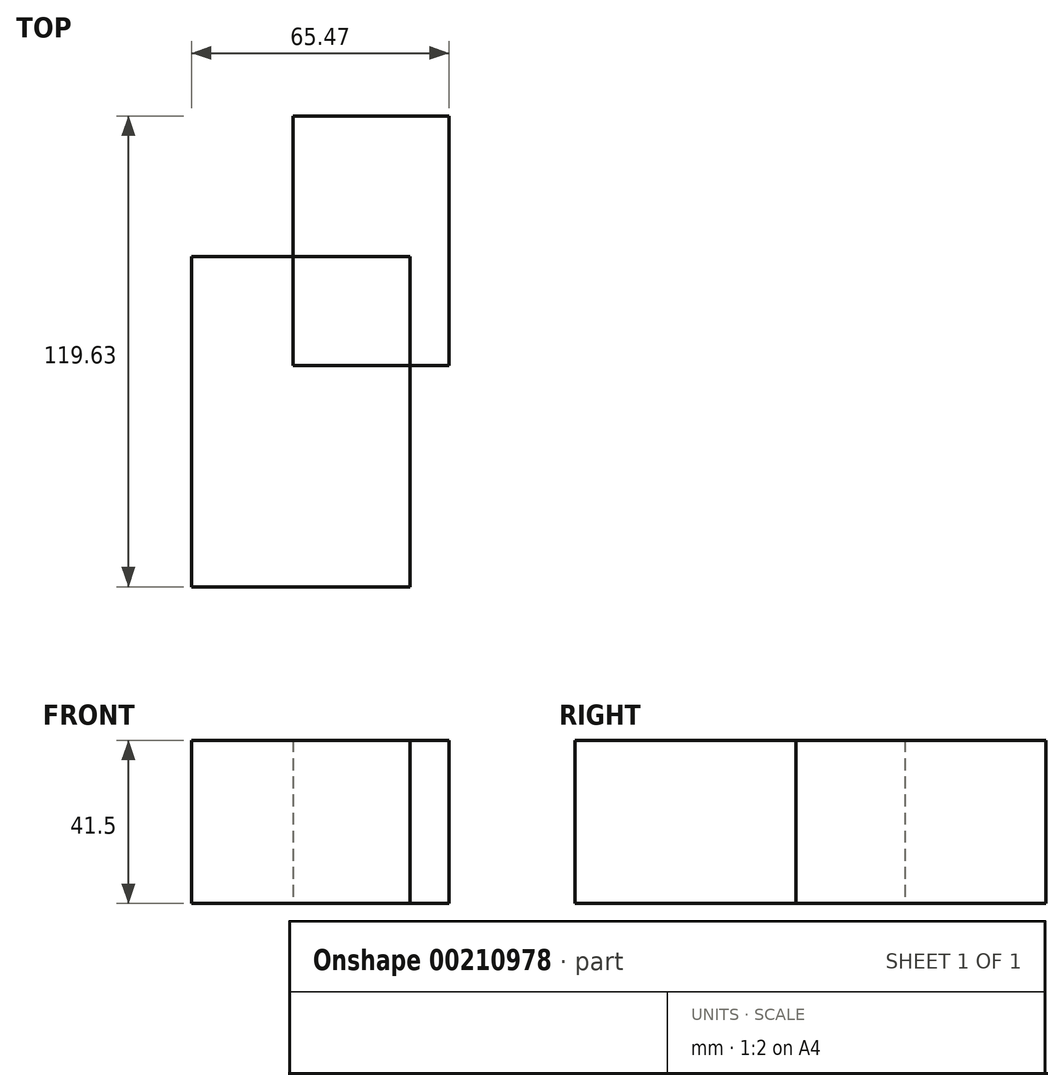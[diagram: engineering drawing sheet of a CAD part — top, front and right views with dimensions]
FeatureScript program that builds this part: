
annotation { "Feature Type Name" : "Feature", "Feature Type Description" : "" }
export const myFeature = defineFeature(function(context is Context, id is Id, definition is map)
    precondition{}
    {
        {
            var Q0;
            Q0=qCreatedBy(makeId("Top.planeOp"),FACE);
            var sketch = newSketch(context, id + "F0", { "sketchPlane" : qUnion([Q0])});
            skLineSegment(sketch, "E0.bottom", {"start": v(-59.9, -48.71) * mm, "end": v(-4.4, -48.71) * mm});
            skLineSegment(sketch, "E0.top", {"start": v(-59.9, 35.14) * mm, "end": v(-4.4, 35.14) * mm});
            skLineSegment(sketch, "E0.left", {"start": v(-59.9, -48.71) * mm, "end": v(-59.9, 35.14) * mm});
            skLineSegment(sketch, "E0.right", {"start": v(-4.4, -48.71) * mm, "end": v(-4.4, 35.14) * mm});
            skLineSegment(sketch, "E1.bottom", {"start": v(-34.03, 7.44) * mm, "end": v(5.57, 7.44) * mm});
            skLineSegment(sketch, "E1.top", {"start": v(-34.03, 70.92) * mm, "end": v(5.57, 70.92) * mm});
            skLineSegment(sketch, "E1.left", {"start": v(-34.03, 7.44) * mm, "end": v(-34.03, 70.92) * mm});
            skLineSegment(sketch, "E1.right", {"start": v(5.57, 7.44) * mm, "end": v(5.57, 70.92) * mm});
            skSolve(sketch);
        }
        {
            var Q0;
            {var subQ1=sQuery(id+"F0.wireOp",EDGE,"E0.bottom");Q0=makeQuery(id+"F0.imprint","IMPRINT",FACE,{"disambiguationData":[TD([[makeQuery(id+"F0.imprint","IMPRINT",EDGE,{"derivedFrom":subQ1}),1.0]])]});}
            var Q1;
            {var subQ0=sQuery(id+"F0.wireOp",EDGE,"E1.top");Q1=makeQuery(id+"F0.imprint","IMPRINT",FACE,{"disambiguationData":[TD([[makeQuery(id+"F0.imprint","IMPRINT",EDGE,{"derivedFrom":subQ0}),-1.0]])]});}
            extrude(context, id + "F1", {"entities" : qUnion([Q0, Q1]), "depth" : 41.5 * mm, "offsetDistance" : 25 * mm});
        }
    });
